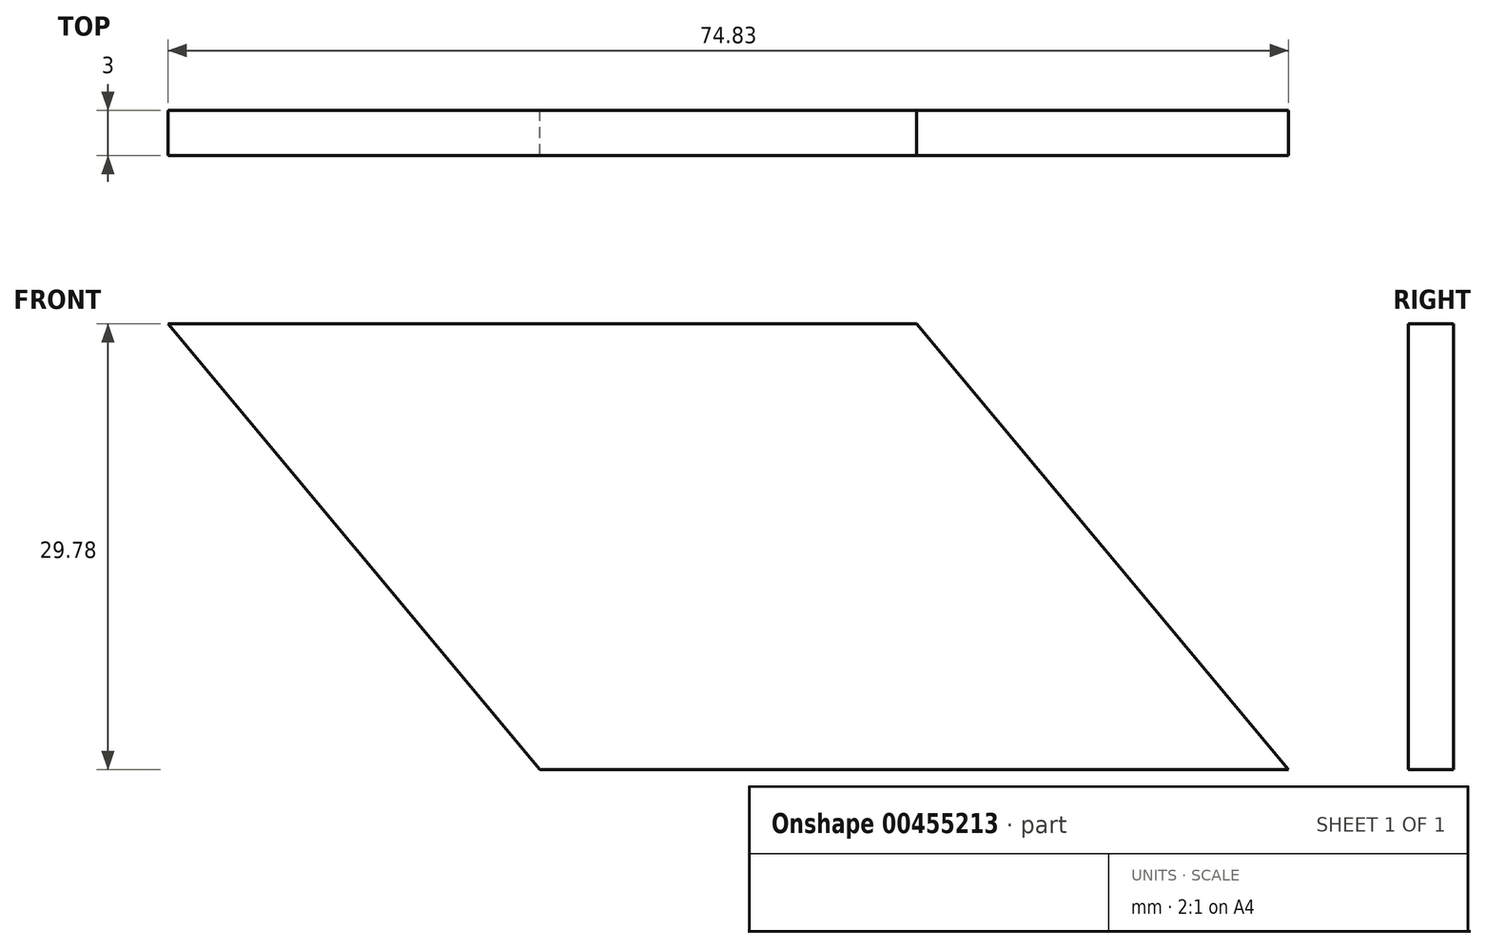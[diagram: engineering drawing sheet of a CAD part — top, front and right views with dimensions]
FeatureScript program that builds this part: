
annotation { "Feature Type Name" : "Feature", "Feature Type Description" : "" }
export const myFeature = defineFeature(function(context is Context, id is Id, definition is map)
    precondition{}
    {
        {
            var Q0;
            Q0=qCreatedBy(makeId("Front.planeOp"),FACE);
            var sketch = newSketch(context, id + "F0", { "sketchPlane" : qUnion([Q0])});
            skLineSegment(sketch, "E0", {"start": v(0, 0) * mm, "end": v(-50, 0) * mm});
            skLineSegment(sketch, "E1", {"start": v(0, 0) * mm, "end": v(-24.83, 29.78) * mm});
            skLineSegment(sketch, "E2", {"start": v(-24.83, 29.78) * mm, "end": v(-74.83, 29.78) * mm});
            skLineSegment(sketch, "E3", {"start": v(-74.83, 29.78) * mm, "end": v(-50, 0) * mm});
            skSolve(sketch);
        }
        {
            var Q0;
            Q0=makeQuery(id+"F0.imprint","IMPRINT",FACE,{"disambiguationData":[TD([[makeQuery(id+"F0.imprint","IMPRINT",EDGE,{"derivedFrom":sQuery(id+"F0.wireOp",EDGE,"E0")}),-1.0]])]});
            extrude(context, id + "F1", {"entities" : qUnion([Q0]), "depth" : 3 * mm, "offsetDistance" : 25 * mm});
        }
        {
            var Q0;
            Q0=qCreatedBy(makeId("Right.planeOp"),FACE);
            cPlane(context, id + "F2", {"entities" : qUnion([Q0]), "cplaneType" : CPlaneType.OFFSET, "offset" : 90 * mm, "oppositeDirection" : true, "width" : 150 * mm, "height" : 150 * mm});
        }
    });
